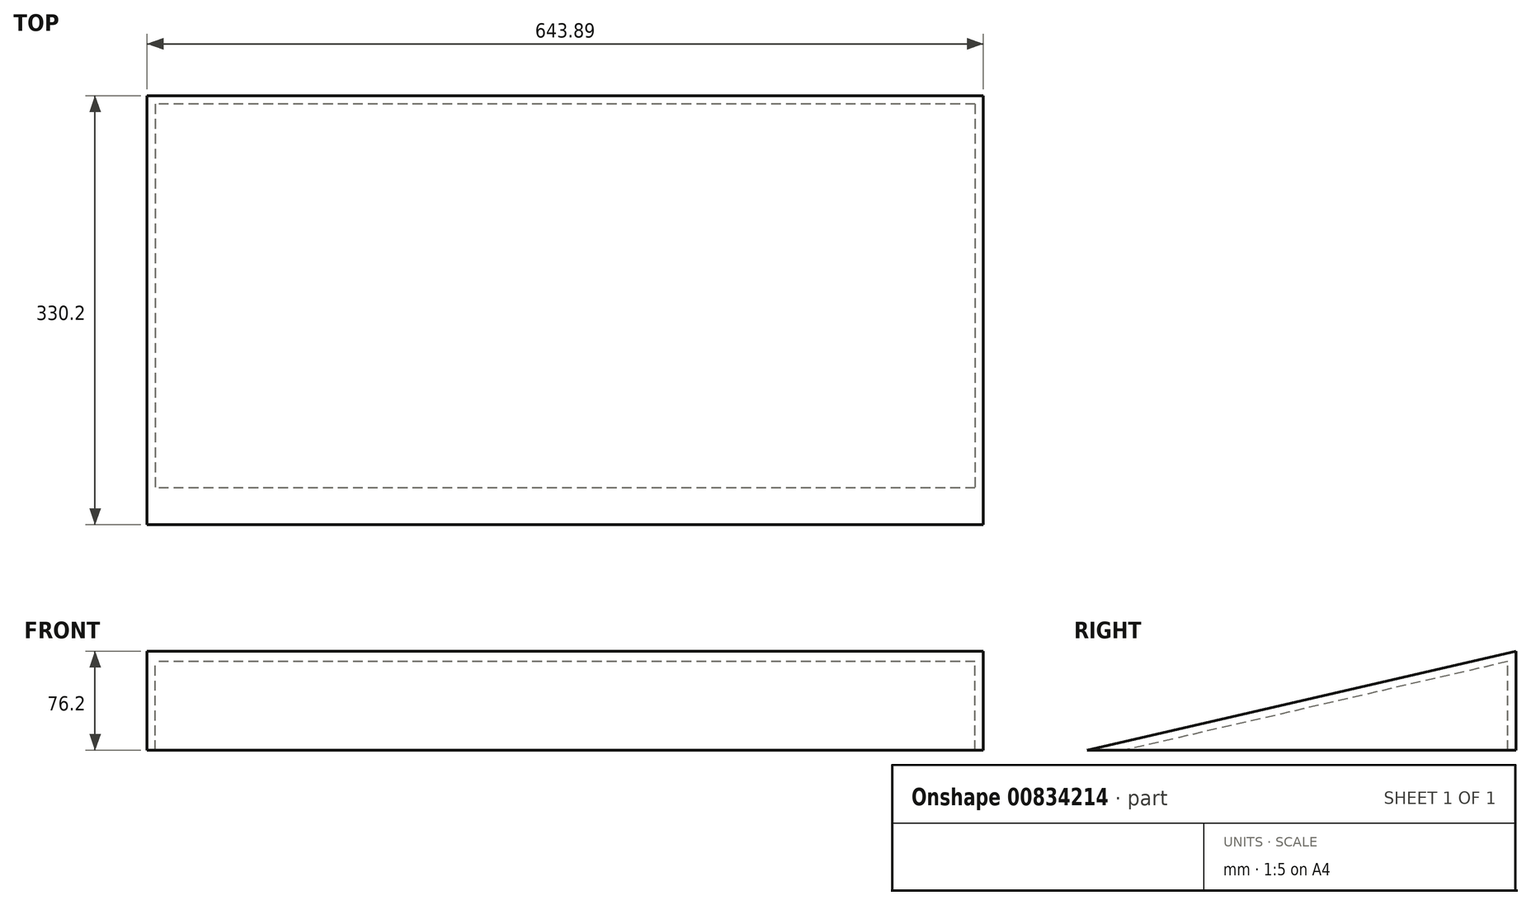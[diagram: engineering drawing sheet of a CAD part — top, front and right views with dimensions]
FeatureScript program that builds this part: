
annotation { "Feature Type Name" : "Feature", "Feature Type Description" : "" }
export const myFeature = defineFeature(function(context is Context, id is Id, definition is map)
    precondition{}
    {
        {
            var Q0;
            Q0=qCreatedBy(makeId("Right.planeOp"),FACE);
            var sketch = newSketch(context, id + "F0", { "sketchPlane" : qUnion([Q0])});
            skLineSegment(sketch, "E0", {"start": v(0, 0) * mm, "end": v(-330.2, 0) * mm});
            skLineSegment(sketch, "E1", {"start": v(0, 0) * mm, "end": v(0, 76.2) * mm});
            skLineSegment(sketch, "E2", {"start": v(0, 76.2) * mm, "end": v(-330.2, 0) * mm});
            skSolve(sketch);
        }
        {
            var Q0;
            Q0=makeQuery(id+"F0.imprint","IMPRINT",FACE,{"disambiguationData":[TD([[makeQuery(id+"F0.imprint","IMPRINT",EDGE,{"derivedFrom":sQuery(id+"F0.wireOp",EDGE,"E0")}),-1.0]])]});
            extrude(context, id + "F1", {"entities" : qUnion([Q0]), "depth" : 643.9 * mm, "offsetDistance" : 25.4 * mm});
        }
        {
            var Q0;
            Q0=makeQuery(id+"F1.opExtrude","SWEPT_FACE",FACE,{"disambiguationData":[OSD([sQuery(id+"F0.wireOp",EDGE,"E0")])]});
            shell(context, id + "F2", {"entities" : qUnion([Q0]), "thickness" : 6.35 * mm});
        }
    });
